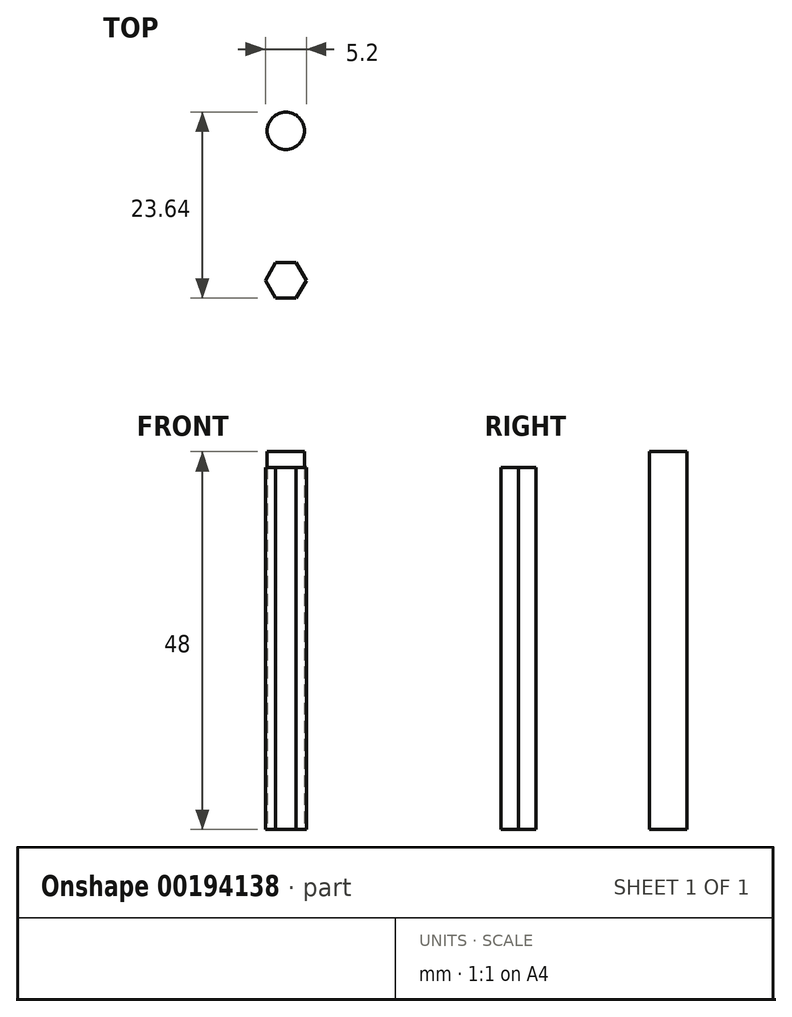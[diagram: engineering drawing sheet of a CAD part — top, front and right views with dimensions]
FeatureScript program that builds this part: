
annotation { "Feature Type Name" : "Feature", "Feature Type Description" : "" }
export const myFeature = defineFeature(function(context is Context, id is Id, definition is map)
    precondition{}
    {
        {
            var Q0;
            Q0=qCreatedBy(makeId("Top.planeOp"),FACE);
            var sketch = newSketch(context, id + "F0", { "sketchPlane" : qUnion([Q0])});
            skCircle(sketch, "E0", {"center": v(0, 0) * mm, "radius": 2.37 * mm});
            skSolve(sketch);
        }
        {
            var Q0;
            Q0 = qSketchRegion(id + "F0", true);
            extrude(context, id + "F1", {"entities" : qUnion([Q0]), "depth" : ((25 - 1) * 2) * mm});
        }
        {
            var Q0;
            Q0=qCreatedBy(makeId("Top.planeOp"),FACE);
            var sketch = newSketch(context, id + "F2", { "sketchPlane" : qUnion([Q0])});
            skCircle(sketch, "E1.cCircle", {"center": v(0, -19.01) * mm, "radius": 2.25 * mm, "construction": true});
            skLineSegment(sketch, "E1.0", {"start": v(1.3, -21.26) * mm, "end": v(-1.3, -21.26) * mm});
            skLineSegment(sketch, "E1.1", {"start": v(-1.3, -21.26) * mm, "end": v(-2.6, -19.01) * mm});
            skLineSegment(sketch, "E1.2", {"start": v(-2.6, -19.01) * mm, "end": v(-1.3, -16.76) * mm});
            skLineSegment(sketch, "E1.3", {"start": v(-1.3, -16.76) * mm, "end": v(1.3, -16.76) * mm});
            skLineSegment(sketch, "E1.4", {"start": v(1.3, -16.76) * mm, "end": v(2.6, -19.01) * mm});
            skLineSegment(sketch, "E1.5", {"start": v(2.6, -19.01) * mm, "end": v(1.3, -21.26) * mm});
            skPoint(sketch, "E1.0.midPoint", {"position": v(0, -21.26) * mm});
            skSolve(sketch);
        }
        {
            var Q0;
            Q0 = qSketchRegion(id + "F2", true);
            extrude(context, id + "F3", {"entities" : qUnion([Q0]), "depth" : (25 * 2 - 4) * mm});
        }
    });
